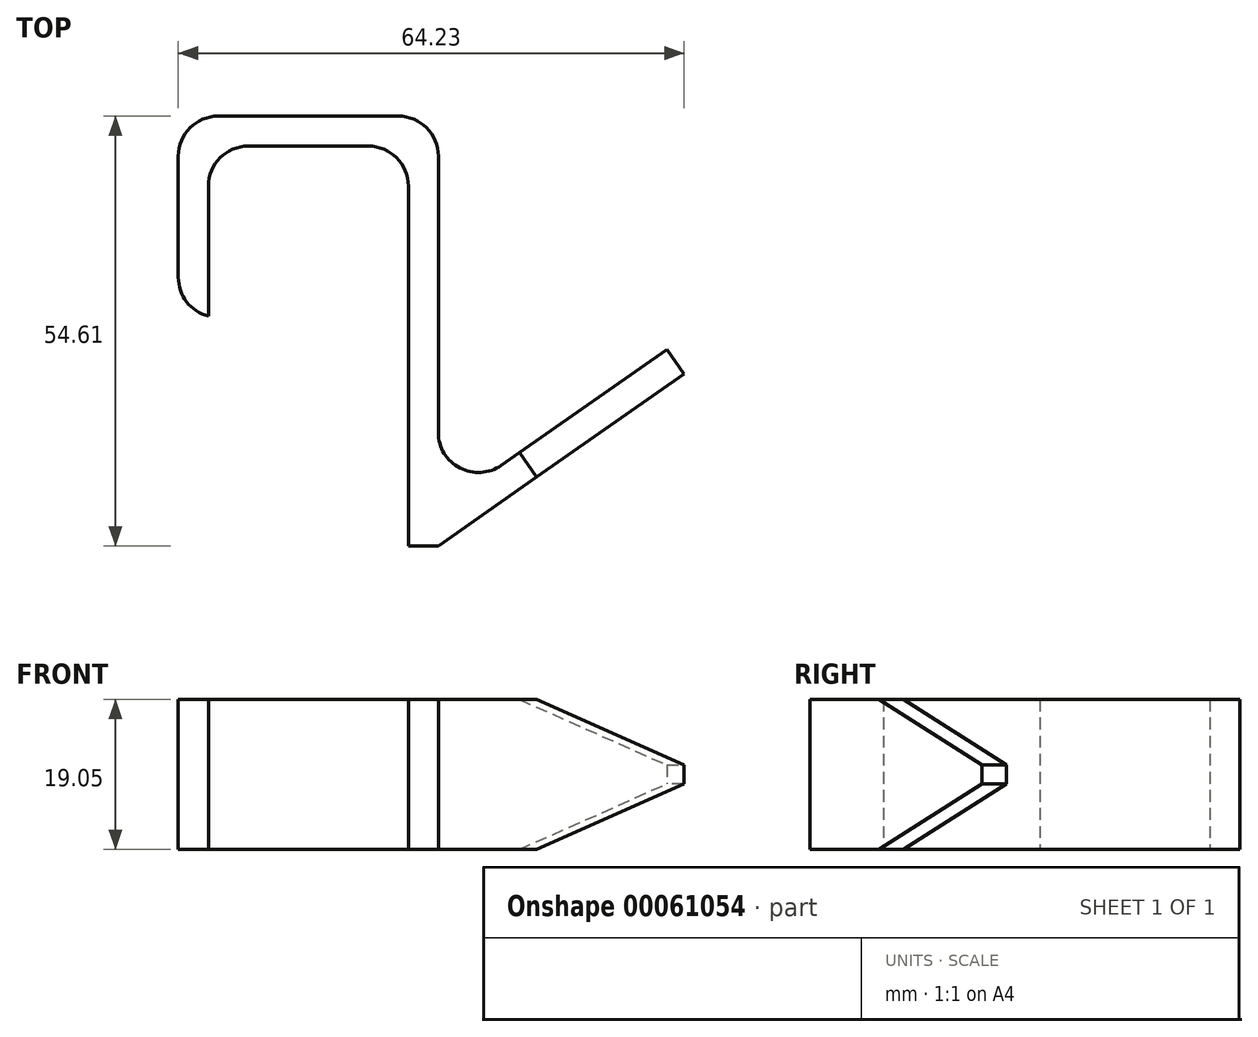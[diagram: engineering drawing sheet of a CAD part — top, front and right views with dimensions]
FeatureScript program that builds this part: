
annotation { "Feature Type Name" : "Feature", "Feature Type Description" : "" }
export const myFeature = defineFeature(function(context is Context, id is Id, definition is map)
    precondition{}
    {
        {
            var Q0;
            Q0=qCreatedBy(makeId("Top.planeOp"),FACE);
            var sketch = newSketch(context, id + "F0", { "sketchPlane" : qUnion([Q0])});
            skLineSegment(sketch, "E0.bottom", {"start": v(-33.02, 4.24) * mm, "end": v(-29.21, 4.24) * mm});
            skLineSegment(sketch, "E0.right", {"start": v(-29.21, 4.24) * mm, "end": v(-29.2, 25.83) * mm});
            skLineSegment(sketch, "E1.bottom", {"start": v(-29.21, 25.83) * mm, "end": v(-3.81, 25.83) * mm});
            skLineSegment(sketch, "E1.top", {"start": v(-33.02, 29.64) * mm, "end": v(0, 29.64) * mm});
            skLineSegment(sketch, "E1.left", {"start": v(-33.02, 4.24) * mm, "end": v(-33.02, 29.64) * mm});
            skLineSegment(sketch, "E2.top", {"start": v(-3.8, -24.97) * mm, "end": v(0, -24.97) * mm});
            skLineSegment(sketch, "E2.left", {"start": v(-3.81, 25.83) * mm, "end": v(-3.8, -24.97) * mm});
            skLineSegment(sketch, "E2.right", {"start": v(0, 29.64) * mm, "end": v(0, -20.32) * mm});
            skLineSegment(sketch, "E3", {"start": v(0, -24.97) * mm, "end": v(31.2, -3.12) * mm});
            skLineSegment(sketch, "E4", {"start": v(31.2, -3.12) * mm, "end": v(29.02, 0) * mm});
            skLineSegment(sketch, "E5", {"start": v(29.02, 0) * mm, "end": v(0, -20.32) * mm});
            skSolve(sketch);
        }
        {
            var Q0;
            Q0=makeQuery(id+"F0.imprint","IMPRINT",FACE,{"disambiguationData":[TD([[makeQuery(id+"F0.imprint","IMPRINT",EDGE,{"derivedFrom":sQuery(id+"F0.wireOp",EDGE,"E0.bottom")}),1.0]])]});
            extrude(context, id + "F1", {"entities" : qUnion([Q0]), "depth" : 19.05 * mm});
        }
        {
            var Q0;
            Q0=makeQuery(id+"F1.opExtrude","SWEPT_EDGE",EDGE,{"disambiguationData":[OSD([sQuery(id+"F0.wireOp",EDGE,"E1.top"),sQuery(id+"F0.wireOp",EDGE,"E1.left")])]});
            var Q1;
            Q1=makeQuery(id+"F1.opExtrude","SWEPT_EDGE",EDGE,{"disambiguationData":[OSD([sQuery(id+"F0.wireOp",EDGE,"E1.top"),sQuery(id+"F0.wireOp",EDGE,"E2.right")])]});
            var Q2;
            Q2=makeQuery(id+"F1.opExtrude","SWEPT_EDGE",EDGE,{"disambiguationData":[OSD([sQuery(id+"F0.wireOp",EDGE,"E0.right"),sQuery(id+"F0.wireOp",EDGE,"E1.bottom")])]});
            var Q3;
            Q3=makeQuery(id+"F1.opExtrude","SWEPT_EDGE",EDGE,{"disambiguationData":[OSD([sQuery(id+"F0.wireOp",EDGE,"E1.bottom"),sQuery(id+"F0.wireOp",EDGE,"E2.left")])]});
            var Q4;
            Q4=makeQuery(id+"F1.opExtrude","SWEPT_EDGE",EDGE,{"disambiguationData":[OSD([sQuery(id+"F0.wireOp",EDGE,"E0.bottom"),sQuery(id+"F0.wireOp",EDGE,"E1.left")])]});
            var Q5;
            Q5=makeQuery(id+"F1.opExtrude","SWEPT_EDGE",EDGE,{"disambiguationData":[OSD([sQuery(id+"F0.wireOp",EDGE,"E2.right"),sQuery(id+"F0.wireOp",EDGE,"E5")])]});
            fillet(context, id + "F2", {"entities" : qUnion([Q0, Q1, Q2, Q3, Q4, Q5]), "radius" : 5.08 * mm, "tangentPropagation" : true, "allowEdgeOverflow" : false});
        }
        {
            var Q0;
            Q0=makeQuery(id+"F1.opExtrude","CAP_EDGE",EDGE,{"disambiguationData":[OSD([sQuery(id+"F0.wireOp",EDGE,"E4")])],"isStart":false});
            var Q1;
            Q1=makeQuery(id+"F1.opExtrude","CAP_EDGE",EDGE,{"disambiguationData":[OSD([sQuery(id+"F0.wireOp",EDGE,"E4")])],"isStart":true});
            chamfer(context, id + "F3", {"entities" : qUnion([Q0, Q1]), "chamferType" : ChamferType.OFFSET_ANGLE, "width" : 22.86 * mm, "oppositeDirection" : false, "angle" : 20 * degree, "tangentPropagation" : true});
        }
    });
